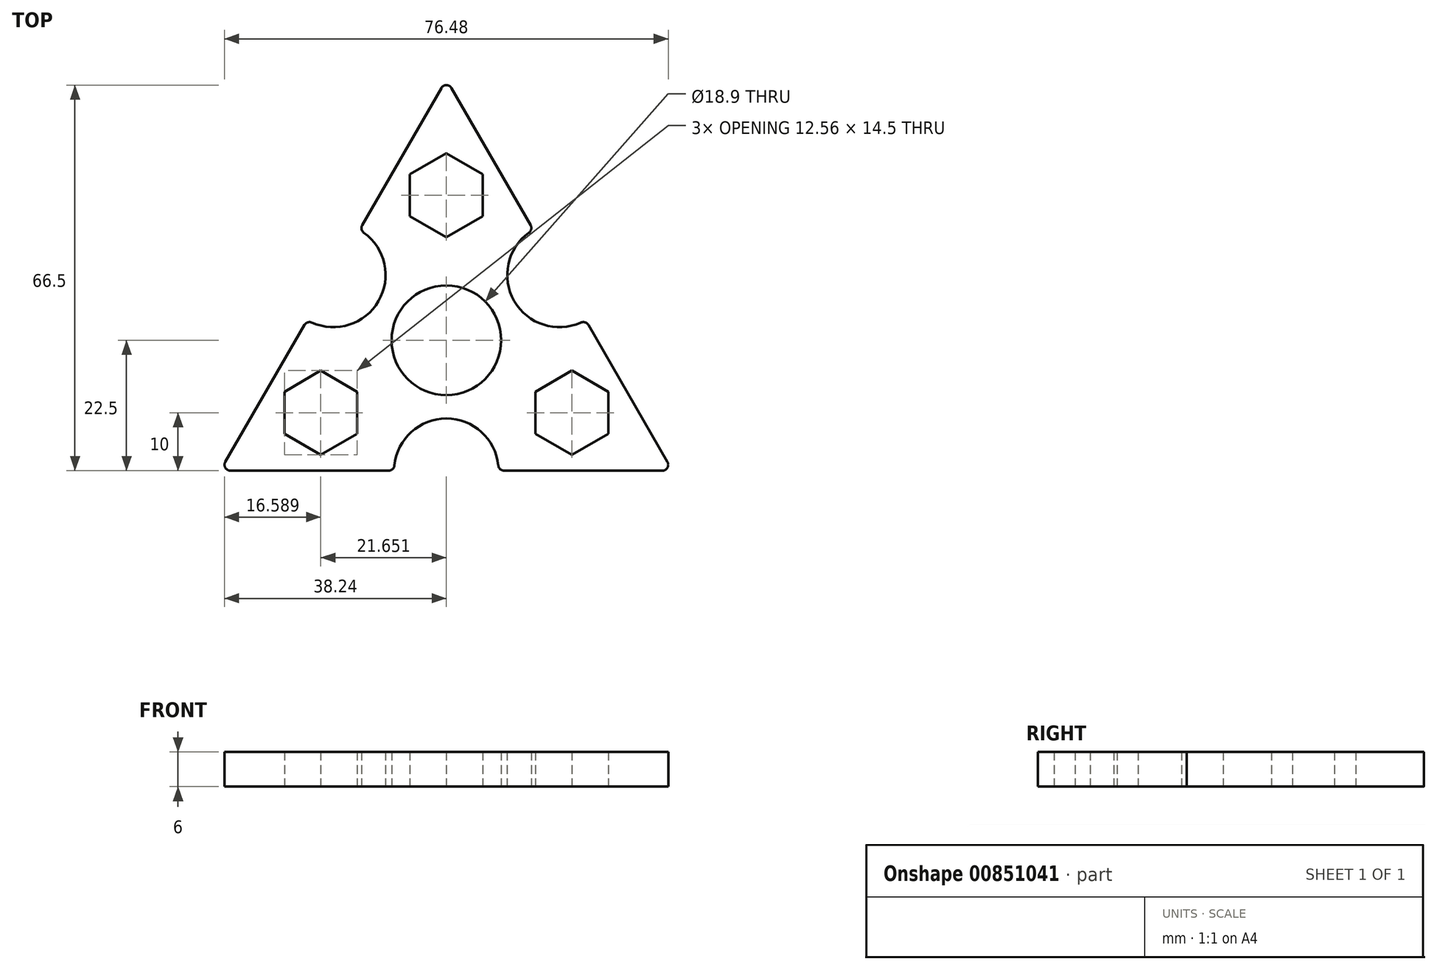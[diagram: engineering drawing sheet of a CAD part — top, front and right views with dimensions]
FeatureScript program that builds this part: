
annotation { "Feature Type Name" : "Feature", "Feature Type Description" : "" }
export const myFeature = defineFeature(function(context is Context, id is Id, definition is map)
    precondition{}
    {
        {
            var Q0;
            Q0=qCreatedBy(makeId("Top.planeOp"),FACE);
            var sketch = newSketch(context, id + "F0", { "sketchPlane" : qUnion([Q0])});
            skCircle(sketch, "E0", {"center": v(0, 0) * mm, "radius": 45 * mm, "construction": true});
            skLineSegment(sketch, "E1.0", {"start": v(0, 45) * mm, "end": v(38.97, -22.5) * mm});
            skLineSegment(sketch, "E1.1", {"start": v(38.97, -22.5) * mm, "end": v(-38.97, -22.5) * mm});
            skLineSegment(sketch, "E1.2", {"start": v(-38.97, -22.5) * mm, "end": v(0, 45) * mm});
            skLineSegment(sketch, "E2", {"start": v(0, 45) * mm, "end": v(0, -22.5) * mm, "construction": true});
            skLineSegment(sketch, "E3.1.0", {"start": v(-38.97, -22.5) * mm, "end": v(19.49, 11.25) * mm, "construction": true});
            skLineSegment(sketch, "E3.2.0", {"start": v(38.97, -22.5) * mm, "end": v(-19.49, 11.25) * mm, "construction": true});
            skArc(sketch, "E4", {"start": v(14.99, 19.04) * mm, "mid": v(11.7, 6.75) * mm, "end": v(23.99, 3.46) * mm});
            skCircle(sketch, "E5", {"center": v(0, 0) * mm, "radius": 9.45 * mm});
            skPoint(sketch, "E6.center", {"position": v(-8.35, -4.82) * mm});
            skArc(sketch, "E7.1.0", {"start": v(-23.99, 3.46) * mm, "mid": v(-11.7, 6.75) * mm, "end": v(-14.99, 19.04) * mm});
            skArc(sketch, "E7.2.0", {"start": v(9, -22.5) * mm, "mid": v(0, -13.5) * mm, "end": v(-9, -22.5) * mm});
            skPoint(sketch, "E8", {"position": v(0, 25) * mm});
            skCircle(sketch, "E9.cCircle", {"center": v(0, 25) * mm, "radius": 7.25 * mm, "construction": true});
            skLineSegment(sketch, "E9.0", {"start": v(0, 32.25) * mm, "end": v(6.28, 28.63) * mm});
            skLineSegment(sketch, "E9.1", {"start": v(6.28, 28.62) * mm, "end": v(6.28, 21.37) * mm});
            skLineSegment(sketch, "E9.2", {"start": v(6.28, 21.37) * mm, "end": v(0, 17.75) * mm});
            skLineSegment(sketch, "E9.3", {"start": v(0, 17.75) * mm, "end": v(-6.28, 21.37) * mm});
            skLineSegment(sketch, "E9.4", {"start": v(-6.28, 21.37) * mm, "end": v(-6.28, 28.62) * mm});
            skLineSegment(sketch, "E9.5", {"start": v(-6.28, 28.62) * mm, "end": v(0, 32.25) * mm});
            skPoint(sketch, "E10.center", {"position": v(4.33, 7.5) * mm});
            skLineSegment(sketch, "E11.1.0", {"start": v(-21.65, -19.75) * mm, "end": v(-27.93, -16.12) * mm});
            skLineSegment(sketch, "E11.1.1", {"start": v(-27.93, -16.12) * mm, "end": v(-27.93, -8.87) * mm});
            skLineSegment(sketch, "E11.1.2", {"start": v(-27.93, -8.87) * mm, "end": v(-21.65, -5.25) * mm});
            skLineSegment(sketch, "E11.1.3", {"start": v(-21.65, -5.25) * mm, "end": v(-15.37, -8.87) * mm});
            skLineSegment(sketch, "E11.1.4", {"start": v(-15.37, -8.87) * mm, "end": v(-15.37, -16.12) * mm});
            skLineSegment(sketch, "E11.1.5", {"start": v(-15.37, -16.12) * mm, "end": v(-21.65, -19.75) * mm});
            skLineSegment(sketch, "E11.2.0", {"start": v(27.93, -8.87) * mm, "end": v(27.93, -16.12) * mm});
            skLineSegment(sketch, "E11.2.1", {"start": v(27.93, -16.13) * mm, "end": v(21.65, -19.75) * mm});
            skLineSegment(sketch, "E11.2.2", {"start": v(21.65, -19.75) * mm, "end": v(15.37, -16.13) * mm});
            skLineSegment(sketch, "E11.2.3", {"start": v(15.37, -16.13) * mm, "end": v(15.37, -8.87) * mm});
            skLineSegment(sketch, "E11.2.4", {"start": v(15.37, -8.87) * mm, "end": v(21.65, -5.25) * mm});
            skLineSegment(sketch, "E11.2.5", {"start": v(21.65, -5.25) * mm, "end": v(27.93, -8.87) * mm});
            skSolve(sketch);
        }
        {
            var Q0;
            {var subQ4=sQuery(id+"F0.wireOp",EDGE,"E4");Q0=makeQuery(id+"F0.imprint","IMPRINT",FACE,{"disambiguationData":[TD([[makeQuery(id+"F0.imprint","IMPRINT",EDGE,{"derivedFrom":subQ4}),-1.0]])]});}
            extrude(context, id + "F1", {"entities" : qUnion([Q0]), "depth" : 6 * mm, "offsetDistance" : 25 * mm});
        }
        {
            var Q0;
            {var subQ0=sQuery(id+"F0.wireOp",EDGE,"E4");var subQ1=sQuery(id+"F0.wireOp",EDGE,"E1.0");Q0=makeQuery(id+"F1.opExtrude","SWEPT_EDGE",EDGE,{"disambiguationData":[OSD([subQ1,subQ0]),TDD([makeQuery(id+"F0.imprint","INTERSECT",VERTEX,{"disambiguationData":[OD(0.0)],"derivedFrom":[subQ1,subQ0]})])]});}
            var Q1;
            {var subQ0=sQuery(id+"F0.wireOp",EDGE,"E7.1.0");var subQ1=sQuery(id+"F0.wireOp",EDGE,"E1.2");Q1=makeQuery(id+"F1.opExtrude","SWEPT_EDGE",EDGE,{"disambiguationData":[OSD([subQ1,subQ0]),TDD([makeQuery(id+"F0.imprint","INTERSECT",VERTEX,{"disambiguationData":[OD(1.0)],"derivedFrom":[subQ1,subQ0]})])]});}
            var Q2;
            {var subQ0=sQuery(id+"F0.wireOp",EDGE,"E7.1.0");var subQ1=sQuery(id+"F0.wireOp",EDGE,"E1.2");Q2=makeQuery(id+"F1.opExtrude","SWEPT_EDGE",EDGE,{"disambiguationData":[OSD([subQ1,subQ0]),TDD([makeQuery(id+"F0.imprint","INTERSECT",VERTEX,{"disambiguationData":[OD(0.0)],"derivedFrom":[subQ1,subQ0]})])]});}
            var Q3;
            {var subQ0=sQuery(id+"F0.wireOp",EDGE,"E7.2.0");var subQ1=sQuery(id+"F0.wireOp",EDGE,"E1.1");Q3=makeQuery(id+"F1.opExtrude","SWEPT_EDGE",EDGE,{"disambiguationData":[OSD([subQ1,subQ0]),TDD([makeQuery(id+"F0.imprint","INTERSECT",VERTEX,{"disambiguationData":[OD(1.0)],"derivedFrom":[subQ1,subQ0]})])]});}
            var Q4;
            {var subQ0=sQuery(id+"F0.wireOp",EDGE,"E7.2.0");var subQ1=sQuery(id+"F0.wireOp",EDGE,"E1.1");Q4=makeQuery(id+"F1.opExtrude","SWEPT_EDGE",EDGE,{"disambiguationData":[OSD([subQ1,subQ0]),TDD([makeQuery(id+"F0.imprint","INTERSECT",VERTEX,{"disambiguationData":[OD(0.0)],"derivedFrom":[subQ1,subQ0]})])]});}
            var Q5;
            {var subQ0=sQuery(id+"F0.wireOp",EDGE,"E4");var subQ1=sQuery(id+"F0.wireOp",EDGE,"E1.0");Q5=makeQuery(id+"F1.opExtrude","SWEPT_EDGE",EDGE,{"disambiguationData":[OSD([subQ1,subQ0]),TDD([makeQuery(id+"F0.imprint","INTERSECT",VERTEX,{"disambiguationData":[OD(1.0)],"derivedFrom":[subQ1,subQ0]})])]});}
            fillet(context, id + "F2", {"entities" : qUnion([Q0, Q1, Q2, Q3, Q4, Q5]), "radius" : 1 * mm, "tangentPropagation" : true, "allowEdgeOverflow" : false});
        }
        {
            var Q0;
            Q0=makeQuery(id+"F1.opExtrude","SWEPT_EDGE",EDGE,{"disambiguationData":[OSD([sQuery(id+"F0.wireOp",EDGE,"E1.0"),sQuery(id+"F0.wireOp",EDGE,"E1.2")])]});
            var Q1;
            Q1=makeQuery(id+"F1.opExtrude","SWEPT_EDGE",EDGE,{"disambiguationData":[OSD([sQuery(id+"F0.wireOp",EDGE,"E1.0"),sQuery(id+"F0.wireOp",EDGE,"E1.1")])]});
            var Q2;
            Q2=makeQuery(id+"F1.opExtrude","SWEPT_EDGE",EDGE,{"disambiguationData":[OSD([sQuery(id+"F0.wireOp",EDGE,"E1.1"),sQuery(id+"F0.wireOp",EDGE,"E1.2")])]});
            fillet(context, id + "F3", {"entities" : qUnion([Q0, Q1, Q2]), "radius" : 1 * mm, "tangentPropagation" : true, "allowEdgeOverflow" : false});
        }
    });
